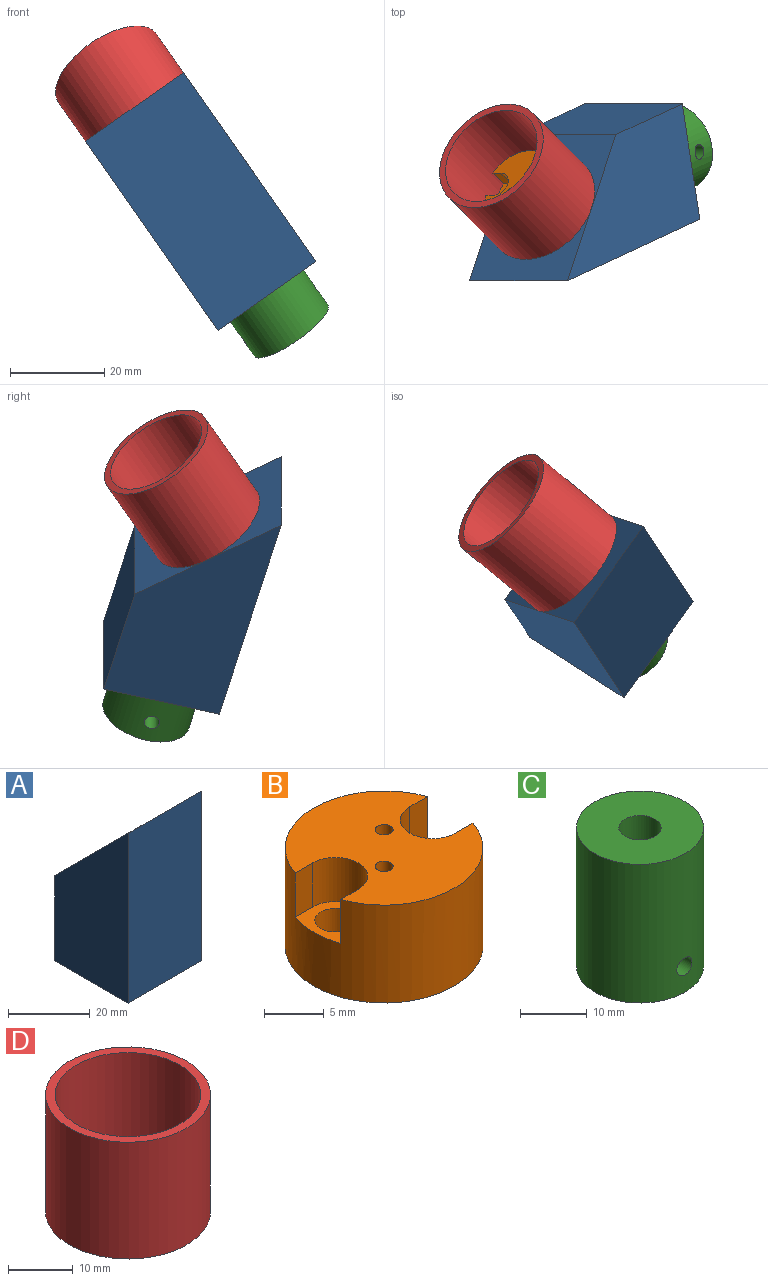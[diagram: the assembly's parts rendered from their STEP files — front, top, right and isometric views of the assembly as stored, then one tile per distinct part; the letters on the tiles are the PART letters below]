
ASSEMBLY  parts=4 mates=3
PART A: 9 faces, bbox 25.4x25.4x50.8 mm
  f0: plane 25.4x25.4mm, normal (0,0,-1), area 360.1mm2, adj f1,f2,f3,f4,f7
  f1: plane 50.8x25.4mm, normal (-1,0,0), area 967.7mm2, adj f0,f2,f4,f5
  f2: plane 50.8x25.4mm, normal (0,-1,0), area 1290.3mm2, adj f0,f1,f3,f5
  f3: plane 50.8x25.4mm, normal (1,0,0), area 967.7mm2, adj f0,f2,f4,f5
  f4: plane 25.4x25.4mm, normal (0,1,0), area 645.2mm2, adj f0,f1,f3,f5
  f5: plane 25.4x25.4mm, normal (0,0.71,0.71), area 867.6mm2, adj f1,f2,f3,f4,f6
  f6: cylinder r=3.17mm len=28.62mm, axis (0,0,-1), area 506.7mm2, adj f5,f8
  f7: cylinder r=9.53mm len=19.05mm, axis (0,0,-1), area 760.1mm2, adj f0,f8
  f8: plane 19.05x19.05mm, normal (0,0,-1), area 253.4mm2, adj f6,f7
PART B: 15 faces, bbox 16.5x16.5x10 mm
  f0: plane 4.5x2.05mm, normal (0,1,0), area 9.2mm2, adj f4,f7,f9,f12
  f1: plane 4.5x2.05mm, normal (0,1,0), area 9.2mm2, adj f2,f4,f9,f14
  f2: cylinder r=2.7mm len=5.4mm, axis (0,0,-1), area 38.2mm2, adj f1,f3,f9,f14
  f3: plane 4.5x2.05mm, normal (0,-1,0), area 9.2mm2, adj f2,f4,f9,f14
  f4: cylinder r=8.25mm len=16.5mm, axis (0,0,-1), area 468.9mm2, adj f0,f1,f3,f5,f9,f10,f12,f14
  f5: plane 4.5x2.05mm, normal (0,-1,0), area 9.2mm2, adj f4,f7,f9,f12
  f6: cylinder r=0.75mm len=10mm, axis (0,0,-1), area 47.1mm2, adj f9,f10
  f7: cylinder r=2.7mm len=5.4mm, axis (0,0,-1), area 38.2mm2, adj f0,f5,f9,f12
  f8: cylinder r=0.75mm len=10mm, axis (0,0,-1), area 47.1mm2, adj f9,f10
  f9: plane 16.5x15.59mm, normal (0,0,1), area 162mm2, adj f0,f1,f2,f3,f4,f5,f6,f7
  f10: plane 16.5x16.5mm, normal (0,0,-1), area 192.1mm2, adj f4,f6,f8,f11,f13
  f11: cylinder r=1.7mm len=5.5mm, axis (0,0,-1), area 58.7mm2, adj f10,f12
  f12: plane 5.4x5.2mm, normal (0,0,1), area 15.1mm2, adj f0,f4,f5,f7,f11
  f13: cylinder r=1.7mm len=5.5mm, axis (0,0,-1), area 58.7mm2, adj f10,f14
  f14: plane 5.4x5.2mm, normal (0,0,1), area 15.1mm2, adj f1,f2,f3,f4,f13
PART C: 6 faces, bbox 19.1x19.1x25.4 mm
  f0: cylinder r=9.53mm len=25.4mm, axis (0,0,1), area 1504.3mm2, adj f1,f2,f4,f5
  f1: plane 19.05x19.05mm, normal (0,0,-1), area 253.4mm2, adj f0,f3
  f2: plane 19.05x19.05mm, normal (0,0,1), area 253.4mm2, adj f0,f3
  f3: cylinder r=3.17mm len=25.4mm, axis (0,0,1), area 490.3mm2, adj f1,f2,f4,f5
  f4: cylinder r=1.59mm len=6.78mm, axis (0,-1,0), area 64.8mm2, adj f0,f3
  f5: cylinder r=1.59mm len=6.78mm, axis (0,-1,0), area 64.8mm2, adj f0,f3
PART D: 4 faces, bbox 25.4x25.4x22 mm
  f0: cylinder r=11.2mm len=22.4mm, axis (0,0,-1), area 1548.2mm2, adj f2,f3
  f1: cylinder r=12.7mm len=25.4mm, axis (0,0,-1), area 1755.5mm2, adj f2,f3
  f2: plane 25.4x25.4mm, normal (0,0,1), area 112.6mm2, adj f0,f1
  f3: plane 25.4x25.4mm, normal (0,0,-1), area 112.6mm2, adj f0,f1
PLACE A rot(axis=(0.38,-0.92,0.12),38deg) t=(-13.89,19.04,71.97)mm
PLACE B rot(axis=(-0.63,-0.75,-0.2),45.8deg) t=(-83.88,28.47,74.21)mm
PLACE C rot(axis=(0.42,-0.17,-0.89),91.7deg) t=(-77.84,-19.1,30.77)mm
PLACE D rot(axis=(-0.29,0.25,0.92),171.1deg) t=(-152.75,-9.74,52.91)mm
MATE fastened C.f0 <-> A.f6  axis (-0.55,-0.26,0.79) through (-69.8,35.04,54.11)mm
MATE fastened A.f5 <-> B.f4  axis (-0.5,0.5,0.71) through (-83.88,28.47,74.21)mm
MATE fastened A.f5 <-> D.f0  axis (-0.5,0.5,0.71) through (-83.88,28.47,74.21)mm
